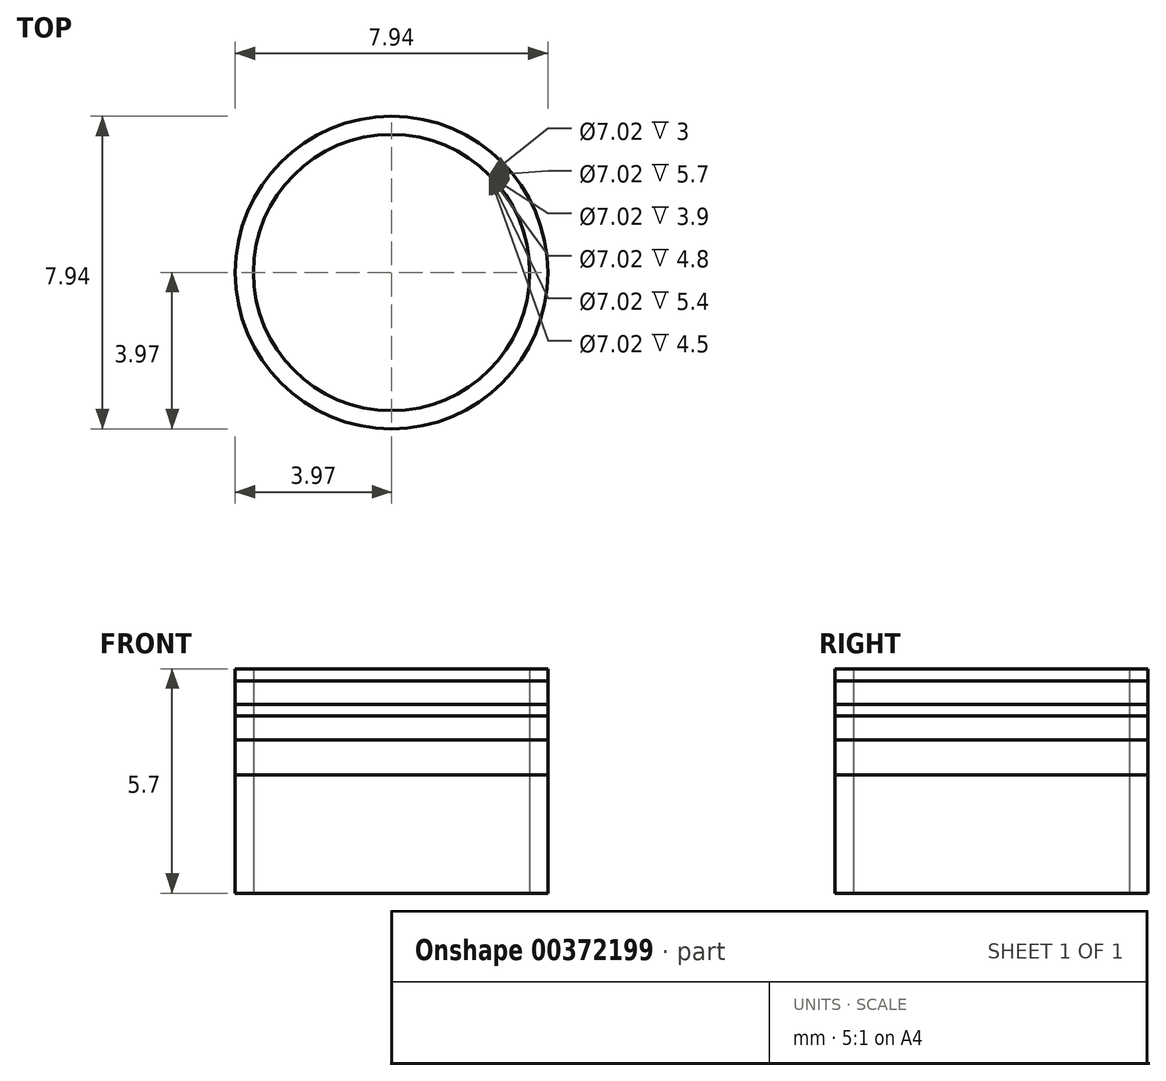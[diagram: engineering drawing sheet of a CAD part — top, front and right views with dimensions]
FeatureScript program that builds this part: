
annotation { "Feature Type Name" : "Feature", "Feature Type Description" : "" }
export const myFeature = defineFeature(function(context is Context, id is Id, definition is map)
    precondition{}
    {
        {
            var Q0;
            Q0=qCreatedBy(makeId("Top.planeOp"),FACE);
            var sketch = newSketch(context, id + "F0", { "sketchPlane" : qUnion([Q0])});
            skCircle(sketch, "E0", {"center": v(0, 0) * mm, "radius": 1.32 * mm});
            skCircle(sketch, "E1", {"center": v(0, 0) * mm, "radius": 1.17 * mm});
            skSolve(sketch);
        }
        {
            var Q0;
            Q0=makeQuery(id+"F0.imprint","IMPRINT",FACE,{"disambiguationData":[TD([[makeQuery(id+"F0.imprint","IMPRINT",EDGE,{"derivedFrom":sQuery(id+"F0.wireOp",EDGE,"E0")}),1.0]])]});
            extrude(context, id + "F1", {"entities" : qUnion([Q0]), "depth" : 1.5 * mm});
        }
        {
            var Q0;
            Q0=makeQuery(id+"F0.imprint","IMPRINT",FACE,{"disambiguationData":[TD([[makeQuery(id+"F0.imprint","IMPRINT",EDGE,{"derivedFrom":sQuery(id+"F0.wireOp",EDGE,"E0")}),1.0]])]});
            extrude(context, id + "F2", {"entities" : qUnion([Q0]), "depth" : 1.6 * mm});
        }
        {
            var Q0;
            Q0=makeQuery(id+"F0.imprint","IMPRINT",FACE,{"disambiguationData":[TD([[makeQuery(id+"F0.imprint","IMPRINT",EDGE,{"derivedFrom":sQuery(id+"F0.wireOp",EDGE,"E0")}),1.0]])]});
            extrude(context, id + "F3", {"entities" : qUnion([Q0]), "depth" : 1.8 * mm});
        }
        {
            var Q0;
            Q0=makeQuery(id+"F0.imprint","IMPRINT",FACE,{"disambiguationData":[TD([[makeQuery(id+"F0.imprint","IMPRINT",EDGE,{"derivedFrom":sQuery(id+"F0.wireOp",EDGE,"E0")}),1.0]])]});
            extrude(context, id + "F4", {"entities" : qUnion([Q0]), "depth" : 1.9 * mm});
        }
        {
            var Q0;
            Q0=makeQuery(id+"F0.imprint","IMPRINT",FACE,{"disambiguationData":[TD([[makeQuery(id+"F0.imprint","IMPRINT",EDGE,{"derivedFrom":sQuery(id+"F0.wireOp",EDGE,"E0")}),1.0]])]});
            extrude(context, id + "F5", {"entities" : qUnion([Q0]), "depth" : 1.3 * mm});
        }
        {
            var Q0;
            Q0=makeQuery(id+"F0.imprint","IMPRINT",FACE,{"disambiguationData":[TD([[makeQuery(id+"F0.imprint","IMPRINT",EDGE,{"derivedFrom":sQuery(id+"F0.wireOp",EDGE,"E0")}),1.0]])]});
            extrude(context, id + "F6", {"entities" : qUnion([Q0]), "depth" : 1 * mm});
        }
        {
            var Q0;
            Q0=makeQuery(id+"F1.opExtrude","SWEPT_BODY",BODY,{"disambiguationData":[OSD([sQuery(id+"F0.wireOp",EDGE,"E0"),sQuery(id+"F0.wireOp",EDGE,"E1")])]});
            var Q1;
            Q1=makeQuery(id+"F2.opExtrude","SWEPT_BODY",BODY,{"disambiguationData":[OSD([sQuery(id+"F0.wireOp",EDGE,"E0"),sQuery(id+"F0.wireOp",EDGE,"E1")])]});
            var Q2;
            Q2=makeQuery(id+"F3.opExtrude","SWEPT_BODY",BODY,{"disambiguationData":[OSD([sQuery(id+"F0.wireOp",EDGE,"E0"),sQuery(id+"F0.wireOp",EDGE,"E1")])]});
            var Q3;
            Q3=makeQuery(id+"F4.opExtrude","SWEPT_BODY",BODY,{"disambiguationData":[OSD([sQuery(id+"F0.wireOp",EDGE,"E0"),sQuery(id+"F0.wireOp",EDGE,"E1")])]});
            var Q4;
            Q4=makeQuery(id+"F5.opExtrude","SWEPT_BODY",BODY,{"disambiguationData":[OSD([sQuery(id+"F0.wireOp",EDGE,"E0"),sQuery(id+"F0.wireOp",EDGE,"E1")])]});
            var Q5;
            Q5=makeQuery(id+"F6.opExtrude","SWEPT_BODY",BODY,{"disambiguationData":[OSD([sQuery(id+"F0.wireOp",EDGE,"E0"),sQuery(id+"F0.wireOp",EDGE,"E1")])]});
            var Q6;
            Q6=qCreatedBy(makeId("Origin.pointOp"),VERTEX);
            transform(context, id + "F7", {"entities" : qUnion([Q0, Q1, Q2, Q3, Q4, Q5]), "transformType" : TransformType.SCALE_UNIFORMLY, "scale" : 3, "makeCopy" : false, "scalePoint" : qUnion([Q6])});
        }
    });
